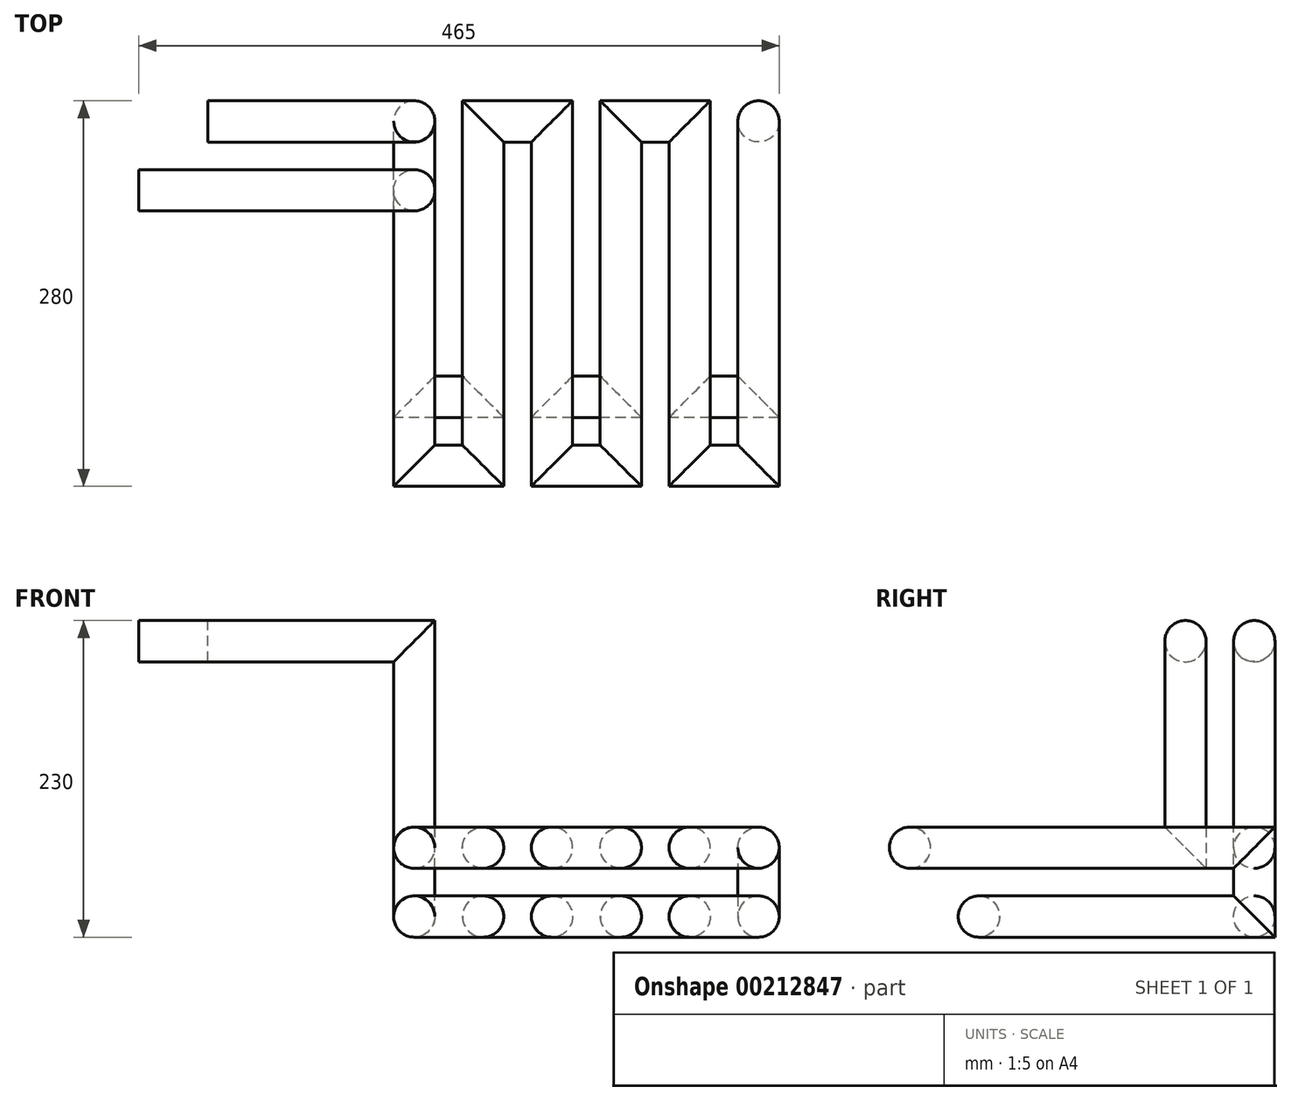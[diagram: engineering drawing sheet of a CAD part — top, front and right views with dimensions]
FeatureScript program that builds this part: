
annotation { "Feature Type Name" : "Feature", "Feature Type Description" : "" }
export const myFeature = defineFeature(function(context is Context, id is Id, definition is map)
    precondition{}
    {
        {
            var Q0;
            Q0=qCreatedBy(makeId("Top.planeOp"),FACE);
            cPlane(context, id + "F0", {"entities" : qUnion([Q0]), "cplaneType" : CPlaneType.OFFSET, "offset" : 50 * mm, "width" : 150 * mm, "height" : 150 * mm});
        }
        {
            var Q0;
            Q0=qCreatedBy(makeId("Top.planeOp"),FACE);
            var sketch = newSketch(context, id + "F1", { "sketchPlane" : qUnion([Q0])});
            skLineSegment(sketch, "E0", {"start": v(-100, 0) * mm, "end": v(-100, -200) * mm});
            skLineSegment(sketch, "E1", {"start": v(-100, -200) * mm, "end": v(-50, -200) * mm});
            skLineSegment(sketch, "E2", {"start": v(-50, -200) * mm, "end": v(-50, 0) * mm});
            skLineSegment(sketch, "E3", {"start": v(-50, 0) * mm, "end": v(0, 0) * mm});
            skLineSegment(sketch, "E4", {"start": v(0, 0) * mm, "end": v(0, -200) * mm});
            skLineSegment(sketch, "E5", {"start": v(0, -200) * mm, "end": v(50, -200) * mm});
            skLineSegment(sketch, "E6", {"start": v(50, -200) * mm, "end": v(50, 0) * mm});
            skLineSegment(sketch, "E7", {"start": v(50, 0) * mm, "end": v(100, 0) * mm});
            skLineSegment(sketch, "E8", {"start": v(100, 0) * mm, "end": v(100, -200) * mm});
            skLineSegment(sketch, "E9", {"start": v(100, -200) * mm, "end": v(150, -200) * mm});
            skLineSegment(sketch, "E10", {"start": v(150, -200) * mm, "end": v(150, 0) * mm});
            skSolve(sketch);
        }
        {
            var Q0;
            Q0=qCreatedBy(makeId("Front.planeOp"),FACE);
            var sketch = newSketch(context, id + "F2", { "sketchPlane" : qUnion([Q0])});
            skLineSegment(sketch, "E11", {"start": v(-100, 0) * mm, "end": v(-100, 200) * mm});
            skLineSegment(sketch, "E12", {"start": v(-100, 200) * mm, "end": v(-250, 200) * mm});
            skSolve(sketch);
        }
        {
            var Q0;
            Q0=qCreatedBy(makeId("Front.planeOp"),FACE);
            cPlane(context, id + "F3", {"entities" : qUnion([Q0]), "cplaneType" : CPlaneType.OFFSET, "offset" : 50 * mm, "width" : 150 * mm, "height" : 150 * mm});
        }
        {
            var Q0;
            Q0=qCreatedBy(makeId("Front.planeOp"),FACE);
            var sketch = newSketch(context, id + "F4", { "sketchPlane" : qUnion([Q0])});
            skLineSegment(sketch, "E13", {"start": v(150, 0) * mm, "end": v(150, 50) * mm});
            skSolve(sketch);
        }
        {
            var Q0;
            Q0=qCreatedBy(id+"F0.planeOp",FACE);
            var sketch = newSketch(context, id + "F5", { "sketchPlane" : qUnion([Q0])});
            skLineSegment(sketch, "E14", {"start": v(150, 0) * mm, "end": v(150, -250) * mm});
            skLineSegment(sketch, "E15", {"start": v(150, -250) * mm, "end": v(100, -250) * mm});
            skLineSegment(sketch, "E16", {"start": v(100, -250) * mm, "end": v(100, 0) * mm});
            skLineSegment(sketch, "E17", {"start": v(100, 0) * mm, "end": v(50, 0) * mm});
            skLineSegment(sketch, "E18", {"start": v(50, 0) * mm, "end": v(50, -250) * mm});
            skLineSegment(sketch, "E19", {"start": v(50, -250) * mm, "end": v(0, -250) * mm});
            skLineSegment(sketch, "E20", {"start": v(0, -250) * mm, "end": v(0, 0) * mm});
            skLineSegment(sketch, "E21", {"start": v(0, 0) * mm, "end": v(-50, 0) * mm});
            skLineSegment(sketch, "E22", {"start": v(-50, 0) * mm, "end": v(-50, -250) * mm});
            skLineSegment(sketch, "E23", {"start": v(-50, -250) * mm, "end": v(-100, -250) * mm});
            skLineSegment(sketch, "E24", {"start": v(-100, -250) * mm, "end": v(-100, -50) * mm});
            skSolve(sketch);
        }
        {
            var Q0;
            Q0=qCreatedBy(id+"F3.planeOp",FACE);
            var sketch = newSketch(context, id + "F6", { "sketchPlane" : qUnion([Q0])});
            skLineSegment(sketch, "E25", {"start": v(-100, 50) * mm, "end": v(-100, 200) * mm});
            skLineSegment(sketch, "E26", {"start": v(-100, 200) * mm, "end": v(-300, 200) * mm});
            skSolve(sketch);
        }
        {
            var Q0;
            Q0=qCreatedBy(makeId("Right.planeOp"),FACE);
            cPlane(context, id + "F7", {"entities" : qUnion([Q0]), "cplaneType" : CPlaneType.OFFSET, "offset" : 300 * mm, "oppositeDirection" : true, "width" : 150 * mm, "height" : 150 * mm});
        }
        {
            var Q0;
            Q0=qCreatedBy(id+"F7.planeOp",FACE);
            var sketch = newSketch(context, id + "F8", { "sketchPlane" : qUnion([Q0])});
            skCircle(sketch, "E27", {"center": v(-50, 200) * mm, "radius": 15 * mm});
            skSolve(sketch);
        }
        {
            var Q0;
            Q0=makeQuery(id+"F8.imprint","IMPRINT",FACE,{"disambiguationData":[TD([[makeQuery(id+"F8.imprint","IMPRINT",EDGE,{"derivedFrom":sQuery(id+"F8.wireOp",EDGE,"E27")}),1.0]])]});
            var Q1;
            Q1=sQuery(id+"F6.wireOp",EDGE,"E26");
            var Q2;
            Q2=sQuery(id+"F6.wireOp",EDGE,"E25");
            var Q3;
            Q3=sQuery(id+"F5.wireOp",EDGE,"E24");
            var Q4;
            Q4=sQuery(id+"F5.wireOp",EDGE,"E23");
            var Q5;
            Q5=sQuery(id+"F5.wireOp",EDGE,"E22");
            var Q6;
            Q6=sQuery(id+"F1.wireOp",EDGE,"E10");
            var Q7;
            Q7=sQuery(id+"F1.wireOp",EDGE,"E9");
            var Q8;
            Q8=sQuery(id+"F1.wireOp",EDGE,"E5");
            var Q9;
            Q9=sQuery(id+"F5.wireOp",EDGE,"E20");
            var Q10;
            Q10=sQuery(id+"F1.wireOp",EDGE,"E2");
            var Q11;
            Q11=sQuery(id+"F1.wireOp",EDGE,"E8");
            var Q12;
            Q12=sQuery(id+"F5.wireOp",EDGE,"E16");
            var Q13;
            Q13=sQuery(id+"F1.wireOp",EDGE,"E4");
            var Q14;
            Q14=sQuery(id+"F1.wireOp",EDGE,"E6");
            var Q15;
            Q15=sQuery(id+"F5.wireOp",EDGE,"E15");
            var Q16;
            Q16=sQuery(id+"F5.wireOp",EDGE,"E19");
            var Q17;
            Q17=sQuery(id+"F4.wireOp",EDGE,"E13");
            var Q18;
            Q18=sQuery(id+"F5.wireOp",EDGE,"E14");
            var Q19;
            Q19=sQuery(id+"F5.wireOp",EDGE,"E18");
            var Q20;
            Q20=sQuery(id+"F1.wireOp",EDGE,"E0");
            var Q21;
            Q21=sQuery(id+"F5.wireOp",EDGE,"E21");
            var Q22;
            Q22=sQuery(id+"F1.wireOp",EDGE,"E1");
            var Q23;
            Q23=sQuery(id+"F1.wireOp",EDGE,"E3");
            var Q24;
            Q24=sQuery(id+"F2.wireOp",EDGE,"E11");
            var Q25;
            Q25=sQuery(id+"F1.wireOp",EDGE,"E7");
            var Q26;
            Q26=sQuery(id+"F5.wireOp",EDGE,"E17");
            var Q27;
            Q27=sQuery(id+"F2.wireOp",EDGE,"E12");
            sweep(context, id + "F9", {"profiles" : qUnion([Q0]), "path" : qUnion([Q1, Q2, Q3, Q4, Q5, Q6, Q7, Q8, Q9, Q10, Q11, Q12, Q13, Q14, Q15, Q16, Q17, Q18, Q19, Q20, Q21, Q22, Q23, Q24, Q25, Q26, Q27])});
        }
    });
